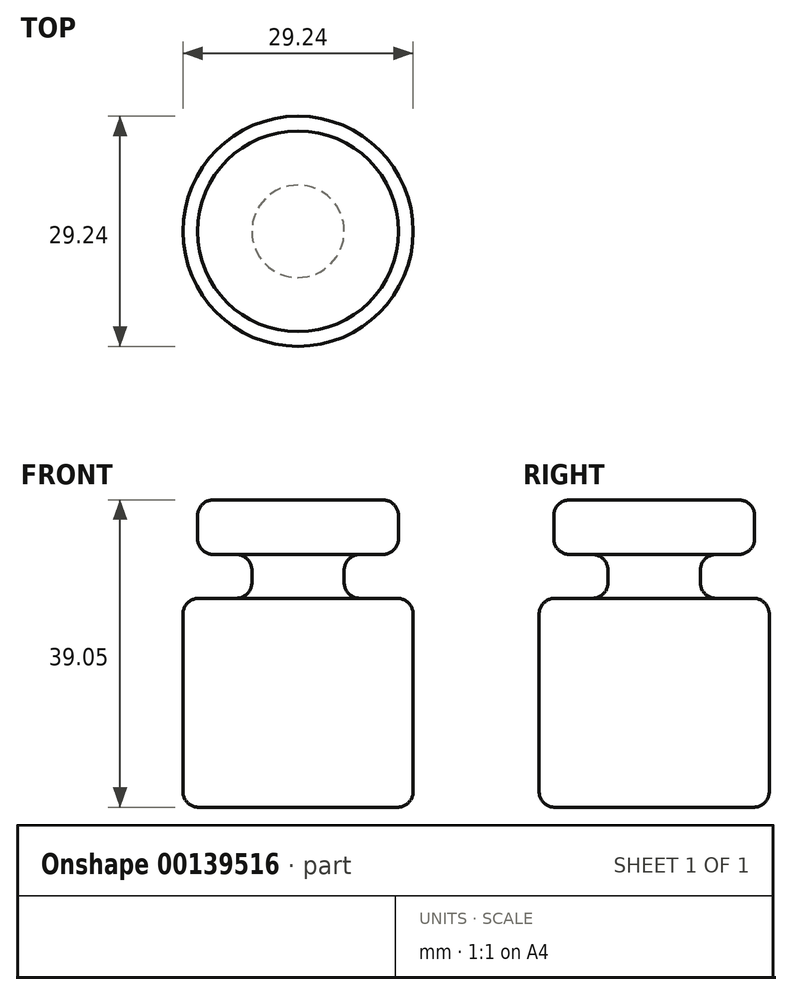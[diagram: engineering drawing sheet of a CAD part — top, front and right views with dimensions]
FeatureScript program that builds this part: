
annotation { "Feature Type Name" : "Feature", "Feature Type Description" : "" }
export const myFeature = defineFeature(function(context is Context, id is Id, definition is map)
    precondition{}
    {
        {
            var Q0;
            Q0=qCreatedBy(makeId("Front.planeOp"),FACE);
            var sketch = newSketch(context, id + "F0", { "sketchPlane" : qUnion([Q0])});
            skLineSegment(sketch, "E0.bottom", {"start": v(0, 42.7) * mm, "end": v(-12.76, 42.7) * mm});
            skLineSegment(sketch, "E0.top", {"start": v(0, 35.77) * mm, "end": v(-12.76, 35.77) * mm});
            skPoint(sketch, "E1.oppositeSnap0", {"position": v(-5.87, 35.77) * mm});
            skLineSegment(sketch, "E1.bottom", {"start": v(0, 35.77) * mm, "end": v(-5.87, 35.77) * mm});
            skLineSegment(sketch, "E1.top", {"start": v(0, 30.2) * mm, "end": v(-5.87, 30.2) * mm});
            skLineSegment(sketch, "E1.right", {"start": v(-5.87, 35.77) * mm, "end": v(-5.87, 30.2) * mm});
            skLineSegment(sketch, "E2.bottom", {"start": v(0, 30.2) * mm, "end": v(-14.62, 30.2) * mm});
            skLineSegment(sketch, "E2.top", {"start": v(0, 3.65) * mm, "end": v(-14.62, 3.65) * mm});
            skLineSegment(sketch, "E2.right", {"start": v(-14.62, 30.2) * mm, "end": v(-14.62, 3.65) * mm});
            skLineSegment(sketch, "E3", {"start": v(0, 42.7) * mm, "end": v(0, 3.65) * mm});
            skPoint(sketch, "E4.orphan", {"position": v(2.75, 35.77) * mm});
            skLineSegment(sketch, "E5", {"start": v(-12.76, 42.7) * mm, "end": v(-12.76, 35.77) * mm});
            skPoint(sketch, "E6.orphan", {"position": v(-14.48, 35.77) * mm});
            skSolve(sketch);
        }
        {
            var Q0;
            Q0 = qSketchRegion(id + "F0", true);
            var Q1;
            Q1=sQuery(id+"F0.wireOp",EDGE,"E3");
            revolve(context, id + "F1", {"entities" : qUnion([Q0]), "axis" : qUnion([Q1]), "revolveType" : RevolveType.FULL});
        }
        {
            var Q0;
            Q0=makeQuery(id+"F1.opRevolve","SWEPT_FACE",FACE,{"disambiguationData":[OSD([sQuery(id+"F0.wireOp",EDGE,"E0.bottom")])]});
            var Q1;
            Q1=makeQuery(id+"F1.opRevolve","SWEPT_FACE",FACE,{"disambiguationData":[OSD([sQuery(id+"F0.wireOp",EDGE,"E2.bottom")])]});
            fillet(context, id + "F2", {"entities" : qUnion([Q0, Q1]), "radius" : 2 * mm, "tangentPropagation" : true, "allowEdgeOverflow" : false});
        }
        {
            var Q0;
            Q0=makeQuery(id+"F1.opRevolve","SWEPT_EDGE",EDGE,{"disambiguationData":[OSD([sQuery(id+"F0.wireOp",EDGE,"E0.top"),sQuery(id+"F0.wireOp",EDGE,"E0.right")])]});
            fillet(context, id + "F3", {"entities" : qUnion([Q0]), "radius" : 2 * mm, "tangentPropagation" : true, "allowEdgeOverflow" : false});
        }
        {
            var Q0;
            Q0=makeQuery(id+"F1.opRevolve","SWEPT_FACE",FACE,{"disambiguationData":[OSD([sQuery(id+"F0.wireOp",EDGE,"E2.right")])]});
            fillet(context, id + "F4", {"entities" : qUnion([Q0]), "radius" : 2 * mm, "tangentPropagation" : true, "allowEdgeOverflow" : false});
        }
    });
